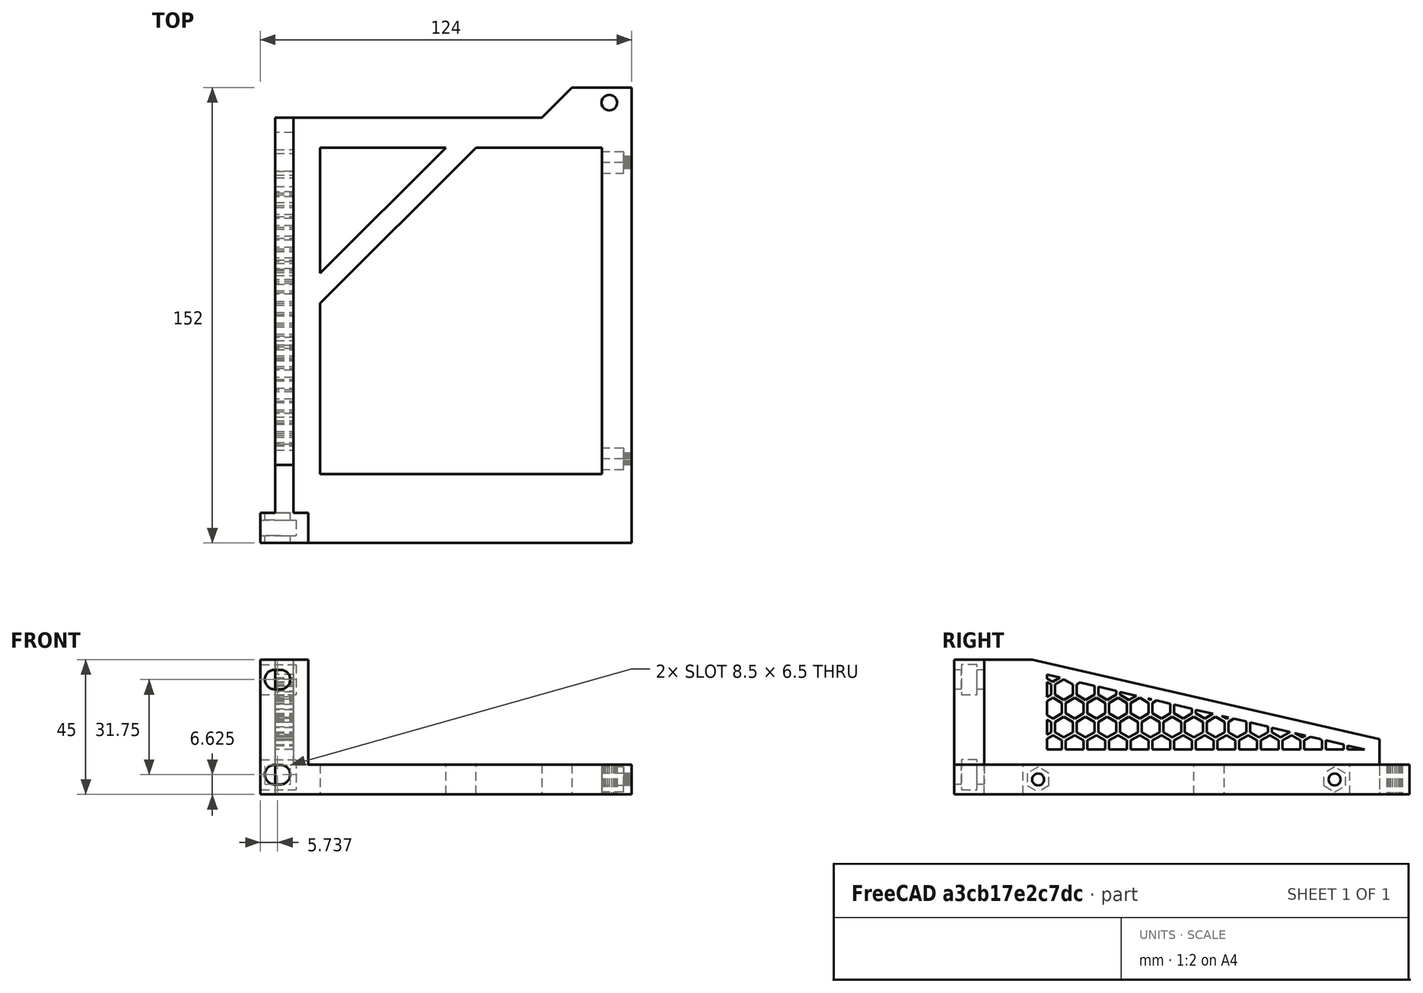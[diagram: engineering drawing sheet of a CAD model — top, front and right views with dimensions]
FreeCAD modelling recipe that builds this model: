
FCSTD DOCUMENT  (FreeCAD 0.21R33771 (Git))
Label: rack
License: All rights reserved
LicenseURL: https://en.wikipedia.org/wiki/All_rights_reserved
objects: Sketcher::SketchObject×3, Part::Feature×2, PartDesign::Pocket×2, Mesh::Feature×1, PartDesign::FeatureBase×1, PartDesign::Pad×1, PartDesign::SubShapeBinder×1, PartDesign::Body×1
note: 14 computed .brp shape members not serialized (recipe doc carries the construction recipe); baked Part::Feature solids carry a one-line shape summary decoded from their .brp

FEATURE [Mesh::Feature] tplink_er7206_left_bracket_Rev2_v24  label="tplink-er7206-left-bracket Rev2 v24"
FEATURE [Part::Feature] tplink_er7206_left_bracket_Rev2_v025
  shape: bbox 240 x 142 x 45 mm, 1794 faces, 0 solids (baked)
FEATURE [Part::Feature] tplink_er7206_left_bracket_Rev2_v025_solid  label="tplink_er7206_left_bracket_Rev2_v025 (Solid)"
  shape: bbox 240 x 142 x 45 mm, 1794 faces (baked)
FEATURE [PartDesign::FeatureBase] BaseFeature
  BaseFeature = -> tplink_er7206_left_bracket_Rev2_v025_solid
FEATURE [Sketcher::SketchObject] Sketch
  FullyConstrained = false
  MapMode = 5
  Placement = pos=(-119,0,0) rot=(0.57735,-0.57735,-0.57735;2.0944rad)
  Support = -> [BaseFeature]
  sketch-geometry (4):
    g0: LineSegment StartX=-154.995 StartY=39.1695 StartZ=0 EndX=28.4134 EndY=39.1695 EndZ=0
    g1: LineSegment StartX=28.4134 StartY=39.1695 StartZ=0 EndX=28.4134 EndY=-45.1734 EndZ=0
    g2: LineSegment StartX=28.4134 StartY=-45.1734 StartZ=0 EndX=-154.995 EndY=-45.1734 EndZ=0
    g3: LineSegment StartX=-154.995 StartY=-45.1734 StartZ=0 EndX=-154.995 EndY=39.1695 EndZ=0
  constraints (8):
    c: Coincident(g0,g1)
    c: Coincident(g1,g2)
    c: Coincident(g2,g3)
    c: Coincident(g3,g0)
    c: Horizontal(g0)
    c: Horizontal(g2)
    c: Vertical(g1)
    c: Vertical(g3)
FEATURE [PartDesign::Pocket] Pocket
  BaseFeature = -> BaseFeature
  Direction = (1,0,0)
  Length = 5
  Length2 = 5
  Profile = -> Sketch
  ReferenceAxis = -> Sketch [N_Axis]
  Reversed = true
  Type = 1
FEATURE [Sketcher::SketchObject] Sketch001
  ExternalGeometry = -> [Pocket]
  FullyConstrained = true
  MapMode = 5
  Placement = pos=(0,0,0) rot=(1,0,0;1.5708rad)
  Support = -> [Pocket]
  expr: Constraints[16] = (254 - 6) / 2
  expr: Constraints[20] = 236.525 mm / 2
  expr: Constraints[47] = 2 * 15.875
  sketch-geometry (21):
    g0: LineSegment StartX=-124 StartY=22.5 StartZ=0 EndX=-108 EndY=22.5 EndZ=0
    g1: LineSegment StartX=-108 StartY=22.5 StartZ=0 EndX=-108 EndY=-12.5 EndZ=0
    g2: LineSegment StartX=-108 StartY=-12.5 StartZ=0 EndX=0 EndY=-12.5 EndZ=0
    g3: LineSegment StartX=0 StartY=-12.5 StartZ=0 EndX=0 EndY=-22.5 EndZ=0
    g4: LineSegment StartX=-124 StartY=-22.5 StartZ=0 EndX=0 EndY=-22.5 EndZ=0
    g5: LineSegment StartX=-124 StartY=22.5 StartZ=0 EndX=-124 EndY=-22.5 EndZ=0
    g6: LineSegment StartX=-118.263 StartY=22.5 StartZ=0 EndX=-118.263 EndY=-22.5 EndZ=0
    g7: ArcOfCircle CenterX=-119.263 CenterY=15.875 CenterZ=0 NormalX=0 NormalY=0 NormalZ=1 AngleXU=0 Radius=3.25 StartAngle=1.5708 EndAngle=4.71239
    g8: ArcOfCircle CenterX=-117.263 CenterY=15.875 CenterZ=0 NormalX=0 NormalY=0 NormalZ=1 AngleXU=0 Radius=3.25 StartAngle=4.71239 EndAngle=7.85398
    g9: LineSegment StartX=-119.263 StartY=12.625 StartZ=0 EndX=-117.263 EndY=12.625 EndZ=0
    g10: LineSegment StartX=-117.263 StartY=19.125 StartZ=0 EndX=-119.263 EndY=19.125 EndZ=0
    g11: LineSegment StartX=-119.263 StartY=15.875 StartZ=0 EndX=-118.263 EndY=15.875 EndZ=0
    g12: LineSegment StartX=-118.263 StartY=15.875 StartZ=0 EndX=-117.263 EndY=15.875 EndZ=0
    g13: LineSegment StartX=-118.263 StartY=-15.875 StartZ=0 EndX=-119.263 EndY=-15.875 EndZ=0
    g14: LineSegment StartX=-118.263 StartY=-15.875 StartZ=0 EndX=-117.263 EndY=-15.875 EndZ=0
    g15: ArcOfCircle CenterX=-119.263 CenterY=-15.875 CenterZ=0 NormalX=0 NormalY=0 NormalZ=1 AngleXU=0 Radius=3.25 StartAngle=1.5708 EndAngle=4.71239
    g16: ArcOfCircle CenterX=-117.263 CenterY=-15.875 CenterZ=0 NormalX=0 NormalY=0 NormalZ=1 AngleXU=0 Radius=3.25 StartAngle=4.71239 EndAngle=7.85398
    g17: LineSegment StartX=-119.263 StartY=-19.125 StartZ=0 EndX=-117.263 EndY=-19.125 EndZ=0
    g18: LineSegment StartX=-117.263 StartY=-12.625 StartZ=0 EndX=-119.263 EndY=-12.625 EndZ=0
    g19: LineSegment StartX=-117.263 StartY=-15.875 StartZ=0 EndX=-117.263 EndY=-22.5 EndZ=0
    g20: LineSegment StartX=-117.263 StartY=15.875 StartZ=0 EndX=-117.263 EndY=22.5 EndZ=0
  constraints (57):
    c: Coincident(g0,g1)
    c: Vertical(g1)
    c: Coincident(g1,g2)
    c: Horizontal(g2)
    c: Coincident(g2,g3)
    c: Coincident(g3,g-3)
    c: Horizontal(g0)
    c: Vertical(g3)
    c: PointOnObject(g-4,g0)
    c: PointOnObject(g-4,g2)
    c: DistanceX(g-4,g0) = 5
    c: Coincident(g4,g3)
    c: Horizontal(g4)
    c: Coincident(g5,g0)
    c: Coincident(g5,g4)
    c: Vertical(g5)
    c: DistanceX(g4,g4) = 124
    c: PointOnObject(g6,g0)
    c: PointOnObject(g6,g4)
    c: Vertical(g6)
    c: DistanceX(g6,g3) = 118.263
    c: Tangent(g7,g9) = -1.5708
    c: Tangent(g9,g8) = -1.5708
    c: Tangent(g8,g10) = -1.5708
    c: Tangent(g10,g7) = -1.5708
    c: Equal(g7,g8)
    c: Horizontal(g9)
    c: Coincident(g11,g7)
    c: Horizontal(g11)
    c: Coincident(g12,g11)
    c: Coincident(g12,g8)
    c: PointOnObject(g11,g6)
    c: Equal(g11,g12)
    c: PointOnObject(g13,g6)
    c: Horizontal(g13)
    c: Coincident(g14,g13)
    c: Horizontal(g14)
    c: Tangent(g15,g17) = -1.5708
    c: Tangent(g17,g16) = -1.5708
    c: Tangent(g16,g18) = -1.5708
    c: Tangent(g18,g15) = -1.5708
    c: Equal(g15,g16)
    c: Coincident(g15,g13)
    c: Equal(g13,g14)
    c: Equal(g13,g11)
    c: Equal(g15,g7)
    c: Coincident(g16,g14)
    c: DistanceY(g13,g11) = 31.75
    c: Coincident(g19,g16)
    c: PointOnObject(g19,g4)
    c: Vertical(g19)
    c: Coincident(g20,g8)
    c: PointOnObject(g20,g0)
    c: Vertical(g20)
    c: Equal(g20,g19)
    c: Diameter(g7) = 6.5
    c: DistanceX(g7,g8) = 2
FEATURE [PartDesign::Pad] Pad
  BaseFeature = -> Pocket
  Direction = (0,-1,2e-16)
  Length = 10
  Length2 = 10
  Profile = -> Sketch001
  ReferenceAxis = -> Sketch001 [N_Axis]
  Type = 0
FEATURE [PartDesign::SubShapeBinder] Binder
  BindCopyOnChange = 0
  BindMode = 0
  ClaimChildren = false
  Context = -> Body [Binder.]
  Fuse = false
  MakeFace = true
  OffsetFill = false
  OffsetIntersection = false
  OffsetJoinType = 0
  OffsetOpenResult = false
  PartialLoad = false
  Placement = pos=(114.3,-21,0) rot=(0,0,1;0rad)
  Relative = true
  Support = -> [tplink_er7206_left_bracket_Rev2_v025_solid]
  _Version = 2
  expr: .Placement.Base.x = (19 in - 10 in) / 2
  expr: .Placement.Base.y = -(5 + 3 + 13)
FEATURE [Sketcher::SketchObject] Sketch002
  ExternalGeometry = -> [Pad]
  FullyConstrained = true
  MapMode = 5
  Placement = pos=(-124,0,0) rot=(0.57735,-0.57735,-0.57735;2.0944rad)
  Support = -> [Pad]
  sketch-geometry (15):
    g0: LineSegment StartX=2.4 StartY=20.875 StartZ=0 EndX=7.6 EndY=20.875 EndZ=0
    g1: LineSegment StartX=7.6 StartY=20.875 StartZ=0 EndX=7.6 EndY=10.875 EndZ=0
    g2: LineSegment StartX=7.6 StartY=10.875 StartZ=0 EndX=2.4 EndY=10.875 EndZ=0
    g3: LineSegment StartX=2.4 StartY=10.875 StartZ=0 EndX=2.4 EndY=20.875 EndZ=0
    g4: LineSegment StartX=2.4 StartY=-10.875 StartZ=0 EndX=7.6 EndY=-10.875 EndZ=0
    g5: LineSegment StartX=7.6 StartY=-10.875 StartZ=0 EndX=7.6 EndY=-20.875 EndZ=0
    g6: LineSegment StartX=7.6 StartY=-20.875 StartZ=0 EndX=2.4 EndY=-20.875 EndZ=0
    g7: LineSegment StartX=2.4 StartY=-20.875 StartZ=0 EndX=2.4 EndY=-10.875 EndZ=0
    g8: LineSegment StartX=2.4 StartY=10.875 StartZ=0 EndX=2.4 EndY=-10.875 EndZ=0
    g9: LineSegment StartX=2.4 StartY=10.875 StartZ=0 EndX=-2.2e-15 EndY=10.875 EndZ=0
    g10: LineSegment StartX=10 StartY=12.625 StartZ=0 EndX=7.6 EndY=12.625 EndZ=0
    g11: LineSegment StartX=10 StartY=19.125 StartZ=0 EndX=7.6 EndY=20.875 EndZ=0
    g12: LineSegment StartX=10 StartY=12.625 StartZ=0 EndX=7.6 EndY=10.875 EndZ=0
    g13: LineSegment StartX=10 StartY=-12.625 StartZ=0 EndX=7.6 EndY=-10.875 EndZ=0
    g14: LineSegment StartX=10 StartY=-19.125 StartZ=0 EndX=7.6 EndY=-20.875 EndZ=0
  constraints (40):
    c: Coincident(g0,g1)
    c: Coincident(g1,g2)
    c: Coincident(g2,g3)
    c: Coincident(g3,g0)
    c: Horizontal(g0)
    c: Horizontal(g2)
    c: Vertical(g1)
    c: Vertical(g3)
    c: Coincident(g4,g5)
    c: Coincident(g5,g6)
    c: Coincident(g6,g7)
    c: Coincident(g7,g4)
    c: Horizontal(g4)
    c: Horizontal(g6)
    c: Vertical(g5)
    c: Vertical(g7)
    c: Equal(g0,g4)
    c: Equal(g5,g1)
    c: DistanceX(g0,g0) = 5.2
    c: DistanceY(g1,g1) = 10
    c: Coincident(g8,g2)
    c: Coincident(g8,g4)
    c: Vertical(g8)
    c: Coincident(g9,g2)
    c: PointOnObject(g9,g-5)
    c: Horizontal(g9)
    c: Coincident(g10,g-3)
    c: PointOnObject(g10,g1)
    c: Horizontal(g10)
    c: Equal(g10,g9)
    c: Coincident(g11,g-3)
    c: Coincident(g11,g0)
    c: Coincident(g12,g10)
    c: Coincident(g12,g1)
    c: Equal(g12,g11)
    c: Coincident(g13,g-4)
    c: Coincident(g13,g4)
    c: Coincident(g14,g-4)
    c: Coincident(g14,g5)
    c: Equal(g14,g13)
FEATURE [PartDesign::Pocket] Pocket001
  BaseFeature = -> Pad
  Direction = (1,0,0)
  Length = 12
  Length2 = 5
  Profile = -> Sketch002
  ReferenceAxis = -> Sketch002 [N_Axis]
  Type = 0
FEATURE [PartDesign::Body] Body
  BaseFeature = -> tplink_er7206_left_bracket_Rev2_v025_solid
  Group = -> [BaseFeature,Sketch,Pocket,Sketch001,Pad,Sketch002,Pocket001]
  Origin = -> Origin
  Tip = -> Pocket001
